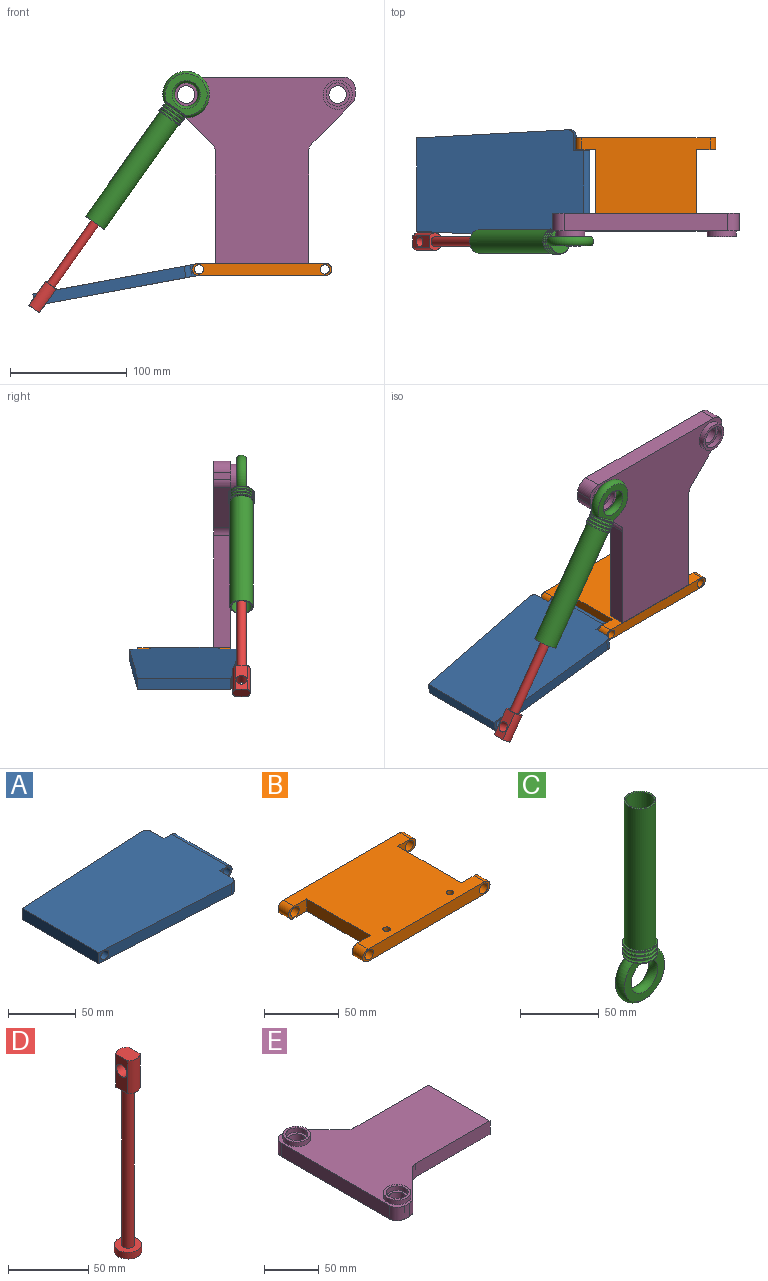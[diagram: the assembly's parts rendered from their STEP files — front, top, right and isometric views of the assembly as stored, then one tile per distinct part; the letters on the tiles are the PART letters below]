
ASSEMBLY  parts=5 mates=5
PART A: 14 faces, bbox 150.1x93.9x10.1 mm
  f0: plane 13x10mm, normal (0,-1,0), area 69mm2, adj f6,f7,f8,f9,f11
  f1: plane 13x10mm, normal (0,1,0), area 69mm2, adj f2,f7,f8,f9,f11
  f2: plane 12.91x10mm, normal (1,0,0), area 129.1mm2, adj f1,f7,f8,f12
  f3: plane 131.83x10.09mm, normal (-0.05,1,0), area 1268.9mm2, adj f4,f7,f8,f10,f12
  f4: plane 80x10mm, normal (-1,0,0), area 800mm2, adj f3,f5,f7,f8
  f5: plane 131.74x10mm, normal (-0.05,-1,0), area 1268.9mm2, adj f4,f7,f8,f10,f13
  f6: plane 12.91x10mm, normal (1,0,0), area 129.1mm2, adj f0,f7,f8,f13
  f7: plane 145x93.82mm, normal (0,0,1), area 12395.5mm2, adj f0,f1,f2,f3,f4,f5,f6,f11
  f8: plane 145x93.82mm, normal (0,0,-1), area 12395.5mm2, adj f0,f1,f2,f3,f4,f5,f6,f11
  f9: cylinder r=4mm len=58mm, axis (0,-1,0), area 1457.7mm2, adj f0,f1
  f10: cylinder r=4mm len=81.05mm, axis (0,1,0), area 2026.4mm2, adj f3,f5
  f11: cylinder r=5mm len=58mm, axis (0,-1,0), area 911.1mm2, adj f0,f1,f7,f8
  f12: cylinder r=5mm len=10mm, axis (0,0,-1), area 81.2mm2, adj f2,f3,f7,f8
  f13: cylinder r=5mm len=10mm, axis (0,0,1), area 81.2mm2, adj f5,f6,f7,f8
PART B: 20 faces, bbox 120x80x10 mm
  f0: plane 120x10mm, normal (0,-1,0), area 1078mm2, adj f8,f9,f10,f13,f16,f17
  f1: plane 17x10mm, normal (0,1,0), area 109mm2, adj f2,f8,f9,f13,f16
  f2: plane 60x10mm, normal (1,0,0), area 600mm2, adj f1,f3,f8,f9
  f3: plane 17x10mm, normal (0,-1,0), area 109mm2, adj f2,f8,f9,f12,f15
  f4: plane 120x10mm, normal (0,1,0), area 1078mm2, adj f8,f9,f11,f12,f14,f15
  f5: plane 17x10mm, normal (0,-1,0), area 109mm2, adj f6,f8,f9,f11,f14
  f6: plane 60x10mm, normal (-1,0,0), area 600mm2, adj f5,f7,f8,f9
  f7: plane 17x10mm, normal (0,1,0), area 109mm2, adj f6,f8,f9,f10,f17
  f8: plane 110x80mm, normal (0,0,1), area 7320.7mm2, adj f0,f1,f2,f3,f4,f5,f6,f7
  f9: plane 110x80mm, normal (0,0,-1), area 7320.7mm2, adj f0,f1,f2,f3,f4,f5,f6,f7
  f10: cylinder r=4mm len=10mm, axis (0,-1,0), area 251.3mm2, adj f0,f7
  f11: cylinder r=4mm len=10mm, axis (0,-1,0), area 251.3mm2, adj f4,f5
  f12: cylinder r=4mm len=10mm, axis (0,-1,0), area 251.3mm2, adj f3,f4
  f13: cylinder r=4mm len=10mm, axis (0,-1,0), area 251.3mm2, adj f0,f1
  f14: cylinder r=5mm len=10mm, axis (0,1,0), area 157.1mm2, adj f4,f5,f8,f9
  f15: cylinder r=5mm len=10mm, axis (0,-1,0), area 157.1mm2, adj f3,f4,f8,f9
  f16: cylinder r=5mm len=10mm, axis (0,-1,0), area 157.1mm2, adj f0,f1,f8,f9
  f17: cylinder r=5mm len=10mm, axis (0,1,0), area 157.1mm2, adj f0,f7,f8,f9
  f18: cylinder r=2.5mm len=10mm, axis (0,0,1), area 157.1mm2, adj f8,f9
  f19: cylinder r=2.5mm len=10mm, axis (0,0,1), area 157.1mm2, adj f8,f9
PART C: 21 faces, bbox 43.3x25.3x156.6 mm
  f0: cylinder r=11mm len=22mm, axis (0,0,-1), area 69.1mm2, adj f1,f6
  f1: plane 22x22mm, normal (0,0,1), area 66mm2, adj f0,f2
  f2: cylinder r=10mm len=110mm, axis (0,0,-1), area 6911.5mm2, adj f1,f3
  f3: plane 20x20mm, normal (0,0,1), area 59.7mm2, adj f2,f4
  f4: cylinder r=9mm len=110mm, axis (0,0,1), area 6220.4mm2, adj f3,f5
  f5: plane 18x18mm, normal (0,0,1), area 254.5mm2, adj f4
  f6: torus R=11mm, axis (0,0,-1), area 204.6mm2, adj f0,f7
  f7: cylinder r=11mm len=22mm, axis (0,0,-1), area 69.1mm2, adj f6,f8
  f8: torus R=11mm, axis (0,0,-1), area 204.6mm2, adj f7,f9
  f9: cylinder r=11mm len=22mm, axis (0,0,-1), area 69.1mm2, adj f8,f10
  f10: torus R=11mm, axis (0,0,-1), area 210.1mm2, adj f9,f16,f17,f18
  f11: torus R=15mm, axis (0,1,0), area 622.6mm2, adj f12,f13
  f12: plane 36x33.09mm, normal (0,1,0), area 525mm2, adj f11,f14,f18,f19
  f13: plane 36x33.09mm, normal (0,-1,0), area 525mm2, adj f11,f15,f18,f20
  f14: plane 19.42x6.5mm, normal (0,0,-1), area 91.3mm2, adj f12,f19
  f15: plane 19.42x6.5mm, normal (0,0,-1), area 91.3mm2, adj f13,f20
  f16: cylinder r=11mm len=21.35mm, axis (0,0,-1), area 14.2mm2, adj f10,f18,f20
  f17: cylinder r=11mm len=21.35mm, axis (0,0,-1), area 14.2mm2, adj f10,f18,f19
  f18: torus R=15mm, axis (0,1,0), area 909mm2, adj f10,f12,f13,f16,f17,f19,f20
  f19: cone r=11mm half-angle=45deg, axis (0,0,1), area 18.5mm2, adj f12,f14,f17,f18
  f20: cone r=11mm half-angle=45deg, axis (0,0,1), area 18.5mm2, adj f13,f15,f16,f18
PART D: 11 faces, bbox 17x17x150 mm
  f0: cylinder r=7.5mm len=25mm, axis (0,0,1), area 308.7mm2, adj f2,f3,f8,f9
  f1: cylinder r=7.5mm len=25mm, axis (0,0,1), area 308.7mm2, adj f2,f3,f8,f9
  f2: plane 15x11mm, normal (0,0,-1), area 98.4mm2, adj f0,f1,f4,f8,f9
  f3: plane 15x11mm, normal (0,0,1), area 148.7mm2, adj f0,f1,f8,f9
  f4: cylinder r=4mm len=120mm, axis (0,0,1), area 3015.9mm2, adj f2,f7
  f5: cylinder r=8.5mm len=17mm, axis (0,0,-1), area 267mm2, adj f6,f7
  f6: plane 17x17mm, normal (0,0,-1), area 227mm2, adj f5
  f7: plane 17x17mm, normal (0,0,1), area 176.7mm2, adj f4,f5
  f8: plane 25x10.2mm, normal (-1,0,0), area 191.3mm2, adj f0,f1,f2,f3,f10
  f9: plane 25x10.2mm, normal (1,0,0), area 191.3mm2, adj f0,f1,f2,f3,f10
  f10: cylinder r=4.5mm len=11mm, axis (1,0,0), area 311mm2, adj f8,f9
PART E: 30 faces, bbox 160x160x20 mm
  f0: plane 20x20mm, normal (0,0,1), area 137.4mm2, adj f16,f21
  f1: plane 20x20mm, normal (0,0,1), area 137.4mm2, adj f17,f18
  f2: plane 34.14x34.14mm, normal (0.71,-0.71,0), area 724.3mm2, adj f10,f11,f24,f29
  f3: plane 95.86x15mm, normal (0,-1,0), area 1437.9mm2, adj f4,f10,f11,f24
  f4: plane 80x15mm, normal (1,0,0), area 1160.7mm2, adj f3,f5,f10,f11,f13,f15
  f5: plane 95.86x15mm, normal (0,1,0), area 1437.9mm2, adj f4,f10,f11,f25
  f6: plane 34.14x34.14mm, normal (0.71,0.71,0), area 724.3mm2, adj f10,f11,f25,f26
  f7: plane 15x5.86mm, normal (0,1,0), area 87.9mm2, adj f10,f11,f26,f27
  f8: plane 140x15mm, normal (-1,0,0), area 2100mm2, adj f10,f11,f27,f28
  f9: plane 15x5.86mm, normal (0,-1,0), area 87.9mm2, adj f10,f11,f28,f29
  f10: plane 160x160mm, normal (0,0,1), area 14975.3mm2, adj f2,f3,f4,f5,f6,f7,f8,f9
  f11: plane 160x160mm, normal (0,0,-1), area 15603.7mm2, adj f2,f3,f4,f5,f6,f7,f8,f9
  f12: cone r=0mm half-angle=59deg, axis (1,0,0), area 22.9mm2, adj f13
  f13: cylinder r=2.5mm len=12mm, axis (1,0,0), area 188.5mm2, adj f4,f12
  f14: cone r=0mm half-angle=59deg, axis (1,0,0), area 22.9mm2, adj f15
  f15: cylinder r=2.5mm len=12mm, axis (1,0,0), area 188.5mm2, adj f4,f14
  f16: cylinder r=7.5mm len=15mm, axis (0,0,1), area 706.9mm2, adj f0,f11
  f17: cylinder r=7.5mm len=15mm, axis (0,0,1), area 706.9mm2, adj f1,f11
  f18: cylinder r=10mm len=20mm, axis (0,0,-1), area 314.2mm2, adj f1,f20
  f19: cylinder r=12.5mm len=25mm, axis (0,0,-1), area 392.7mm2, adj f10,f20
  f20: plane 25x25mm, normal (0,0,1), area 176.7mm2, adj f18,f19
  f21: cylinder r=10mm len=20mm, axis (0,0,-1), area 314.2mm2, adj f0,f23
  f22: cylinder r=12.5mm len=25mm, axis (0,0,-1), area 392.7mm2, adj f10,f23
  f23: plane 25x25mm, normal (0,0,1), area 176.7mm2, adj f21,f22
  f24: cylinder r=10mm len=15mm, axis (0,0,1), area 117.8mm2, adj f2,f3,f10,f11
  f25: cylinder r=10mm len=15mm, axis (0,0,1), area 117.8mm2, adj f5,f6,f10,f11
  f26: cylinder r=10mm len=15mm, axis (0,0,-1), area 117.8mm2, adj f6,f7,f10,f11
  f27: cylinder r=10mm len=15mm, axis (0,0,1), area 235.6mm2, adj f7,f8,f10,f11
  f28: cylinder r=10mm len=15mm, axis (0,0,-1), area 235.6mm2, adj f8,f9,f10,f11
  f29: cylinder r=10mm len=15mm, axis (0,0,-1), area 117.8mm2, adj f2,f9,f10,f11
PLACE A rot(axis=(0,-1,0),10.5deg) t=(-135.6,0,-26.17)mm
PLACE B at identity fixed
PLACE C rot(axis=(0,-1,0),144.7deg) t=(-13.68,-9,137.76)mm
PLACE D rot(axis=(0,-1,0),144.7deg) t=(-48.72,-9,88.36)mm
PLACE E rot(axis=(0.58,0.58,-0.58),120deg) t=(60,15,165)mm
MATE fastened E.f14 <-> B.f19  axis (0,0,-1) through (90,7.5,5)mm
MATE planar C.f11 <-> E.f16  axis (0,1,0) through (-5,-5,150)mm
MATE slider C.f4 <-> D.f5  axis (-0.58,0,-0.82) through (-19.46,-9,129.61)mm
MATE revolute A.f9 <-> B.f10  axis (0,-1,0) through (6,11,0)mm
MATE cylindrical C.f11 <-> E.f16  axis (0,1,0) through (-5,-5,150)mm
